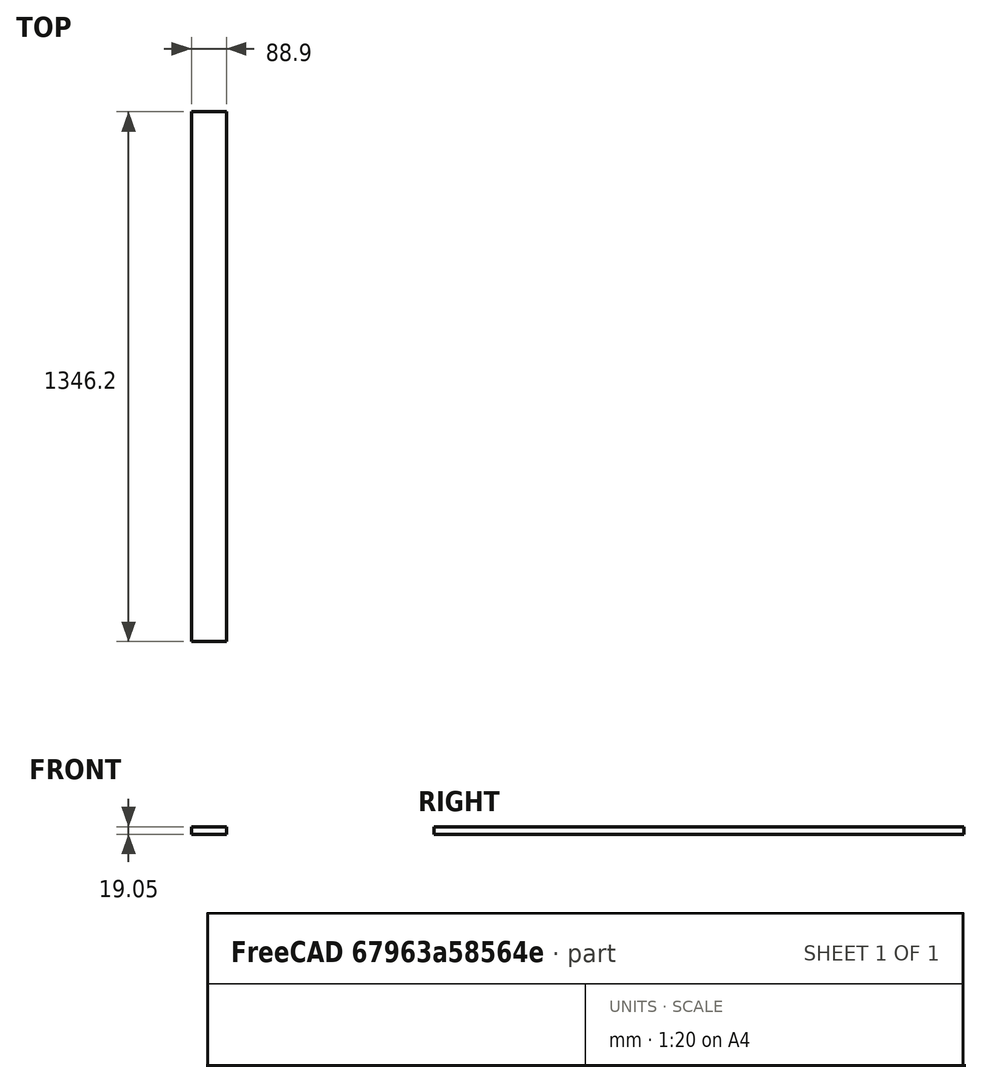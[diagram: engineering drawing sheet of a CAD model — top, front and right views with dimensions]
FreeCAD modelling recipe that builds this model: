
FCSTD DOCUMENT  (FreeCAD 0.18.3R)
Label: wood1x4x53
License: All rights reserved
LicenseURL: http://en.wikipedia.org/wiki/All_rights_reserved
objects: Sketcher::SketchObject×1, PartDesign::Pad×1, PartDesign::Body×1
note: 4 computed .brp shape members not serialized (recipe doc carries the construction recipe); baked Part::Feature solids carry a one-line shape summary decoded from their .brp

FEATURE [Sketcher::SketchObject] Sketch
  MapMode = 5
  Placement = pos=(0,0,0) rot=(1,0,0;1.5708rad)
  Support = -> [XZ_Plane]
  sketch-geometry (4):
    g0: LineSegment StartX=0 StartY=0 StartZ=0 EndX=-88.9 EndY=0 EndZ=0
    g1: LineSegment StartX=-88.9 StartY=0 StartZ=0 EndX=-88.9 EndY=19.05 EndZ=0
    g2: LineSegment StartX=-88.9 StartY=19.05 StartZ=0 EndX=0 EndY=19.05 EndZ=0
    g3: LineSegment StartX=0 StartY=19.05 StartZ=0 EndX=0 EndY=0 EndZ=0
  constraints (11):
    c: Coincident(g0,g1)
    c: Coincident(g1,g2)
    c: Coincident(g2,g3)
    c: Coincident(g3,g0)
    c: Horizontal(g0)
    c: Horizontal(g2)
    c: Vertical(g1)
    c: Vertical(g3)
    c: Coincident(g0,g-1)
    c: DistanceY(g3,g3) = 19.05
    c: DistanceX(g0,g0) = 88.9
FEATURE [PartDesign::Pad] Pad
  Length = 1346.2
  Length2 = 98.425
  Placement = pos=(0,0,0) rot=(1,0,0;1.5708rad)
  Profile = -> Sketch
  Type = 0
FEATURE [PartDesign::Body] Body
  Group = -> [Sketch,Pad]
  Origin = -> Origin
  Tip = -> Pad
